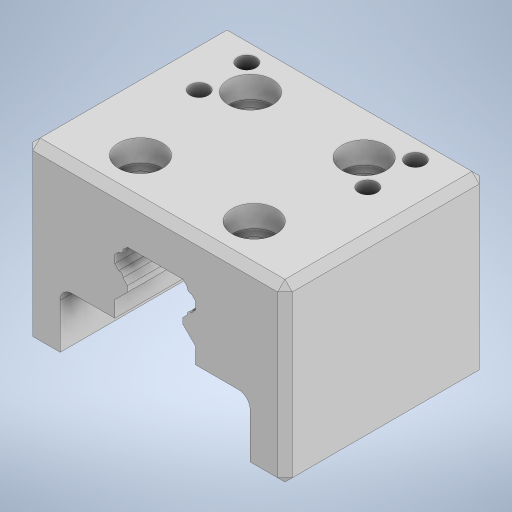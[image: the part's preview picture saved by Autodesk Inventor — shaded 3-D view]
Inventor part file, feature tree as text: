
AUTODESK INVENTOR PART (.ipt)
format: ipt  version: 2023 (Build 270158000, 158)  size: 402,432 bytes
history: native  units: in
note: dims shown in document units (in); Inventor stores cm internally (conversion verified against a paired STEP export)
features: extrude x7, sketch x3, thicken_offset x1, chamfer x1
ambient origin geometry x8: Origin, YZ Plane, XZ Plane, XY Plane, X Axis, Y Axis, Z Axis, Center Point
bodies: Solid1 (feature_tree)
feature tree (12):
  extrude  "Extrusion1"  Depth=2.3622in
  extrude  "Extrusion2"  Depth=0.0197in
  extrude  "Extrusion3"  Depth=0.0787in
  extrude  "Extrusion4"  Depth=0.1969in
  extrude  "Extrusion5"  Depth=0.0787in
  extrude  "Extrusion6"  Depth=0.0787in
  extrude  "Extrusion9"  Depth=2.7874in
  thicken_offset  "Thicken1"
  chamfer  "Chamfer1"  Distance=2.1654in
  sketch  "Sketch4"  dims[d0=0.9843in d1=2.3622in]
  sketch  "Sketch5"  dims[d2=0.0197in d3=0.0197in]
  sketch  "Sketch8"  dims[d4=0.0197in d5=0.0197in d6=0.1969in d7=1.811in d8=0.5118in d9=2.7874in d10=2.1654in d11=1.3937in d12=0.0in d13=1.3937in d14=0.0in d15=0.3937in d16=0.1969in d17=0.0in d18=0.0in d19=0.3937in d20=1.1969in d21=0.0in d22=0.0in d27=0.3937in d28=0.0in d29=0.2687in d31=1.4375in d32=0.0in d34=0.4724in d35=0.2362in d36=0.0in d50=1.3937in d51=0.0394in d52=0.1181in d53=135.0deg d54=0.0787in d55=0.1358in d56=0.689in d57=0.2819in d58=0.0935in d59=0.0525in d60=0.0953in d61=0.3937in d63=0.3937in d64=0.0in d66=0.0394in d67=0.125in d68=0.374in d69=0.689in d70=90.0deg d71=90.0deg d72=0.7874in d73=0.0394in d74=0.5315in d78=1.1811in d79=1.2205in d80=0.5315in d81=0.0787in d82=0.0787in d83=45.0deg]
